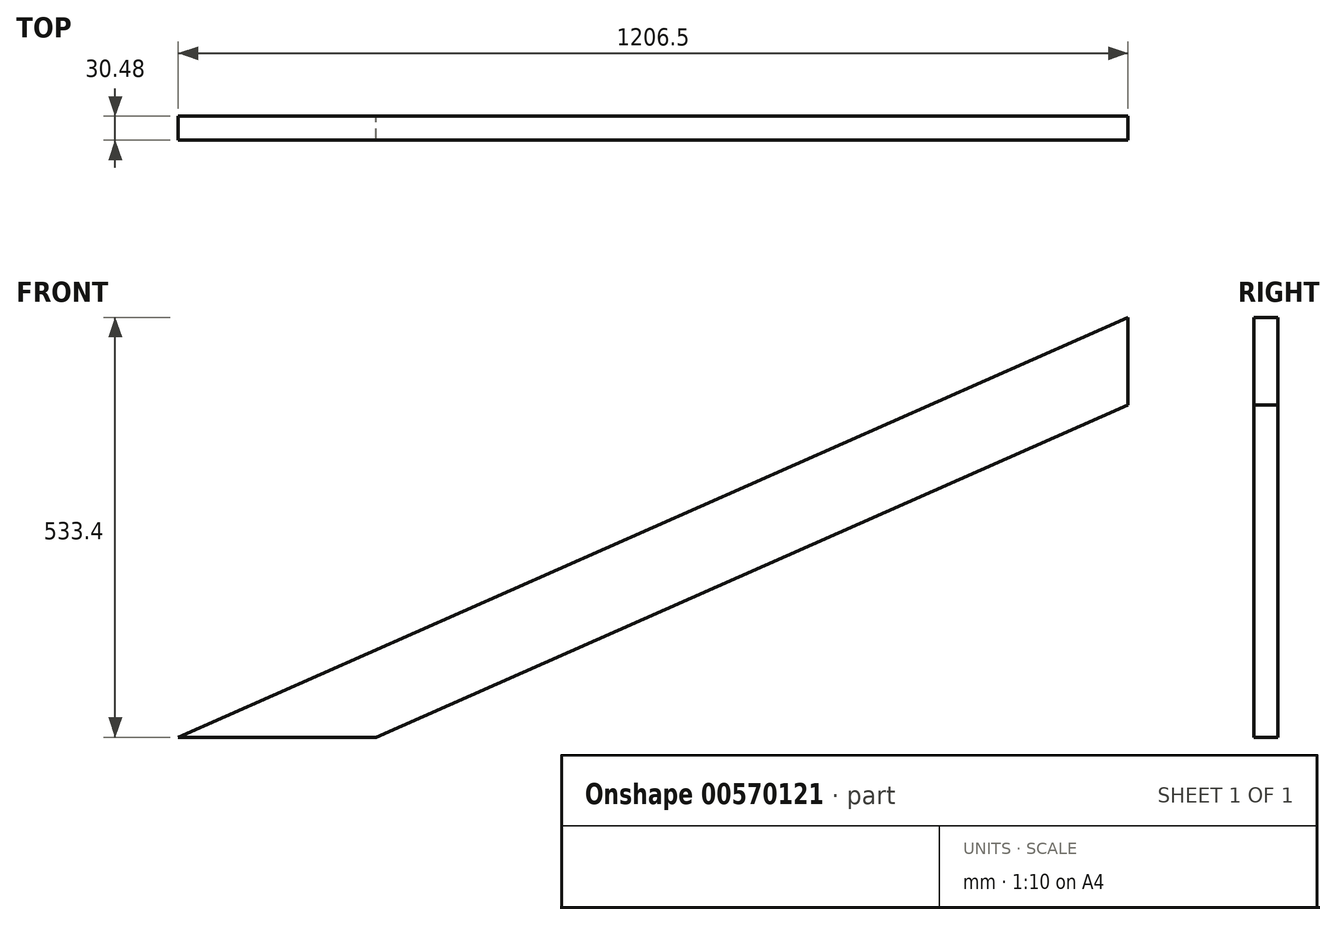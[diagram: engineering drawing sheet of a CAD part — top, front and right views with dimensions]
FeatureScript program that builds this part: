
annotation { "Feature Type Name" : "Feature", "Feature Type Description" : "" }
export const myFeature = defineFeature(function(context is Context, id is Id, definition is map)
    precondition{}
    {
        {
            var Q0;
            Q0=qCreatedBy(makeId("Front.planeOp"),FACE);
            var sketch = newSketch(context, id + "F0", { "sketchPlane" : qUnion([Q0])});
            skLineSegment(sketch, "E0", {"start": v(0, 0) * mm, "end": v(1206.5, 533.4) * mm});
            skLineSegment(sketch, "E1", {"start": v(1206.5, 422.31) * mm, "end": v(251.27, 0) * mm});
            skLineSegment(sketch, "E2", {"start": v(251.27, 0) * mm, "end": v(0, 0) * mm});
            skLineSegment(sketch, "E3", {"start": v(1206.5, 533.4) * mm, "end": v(1206.5, 422.31) * mm});
            skLineSegment(sketch, "E4", {"start": v(1206.5, 422.31) * mm, "end": v(1206.5, -331.81) * mm});
            skSolve(sketch);
        }
        {
            var Q0;
            Q0 = qSketchRegion(id + "F0", true);
            extrude(context, id + "F1", {"entities" : qUnion([Q0]), "depth" : 30.48 * mm, "offsetDistance" : 30.48 * mm});
        }
    });
